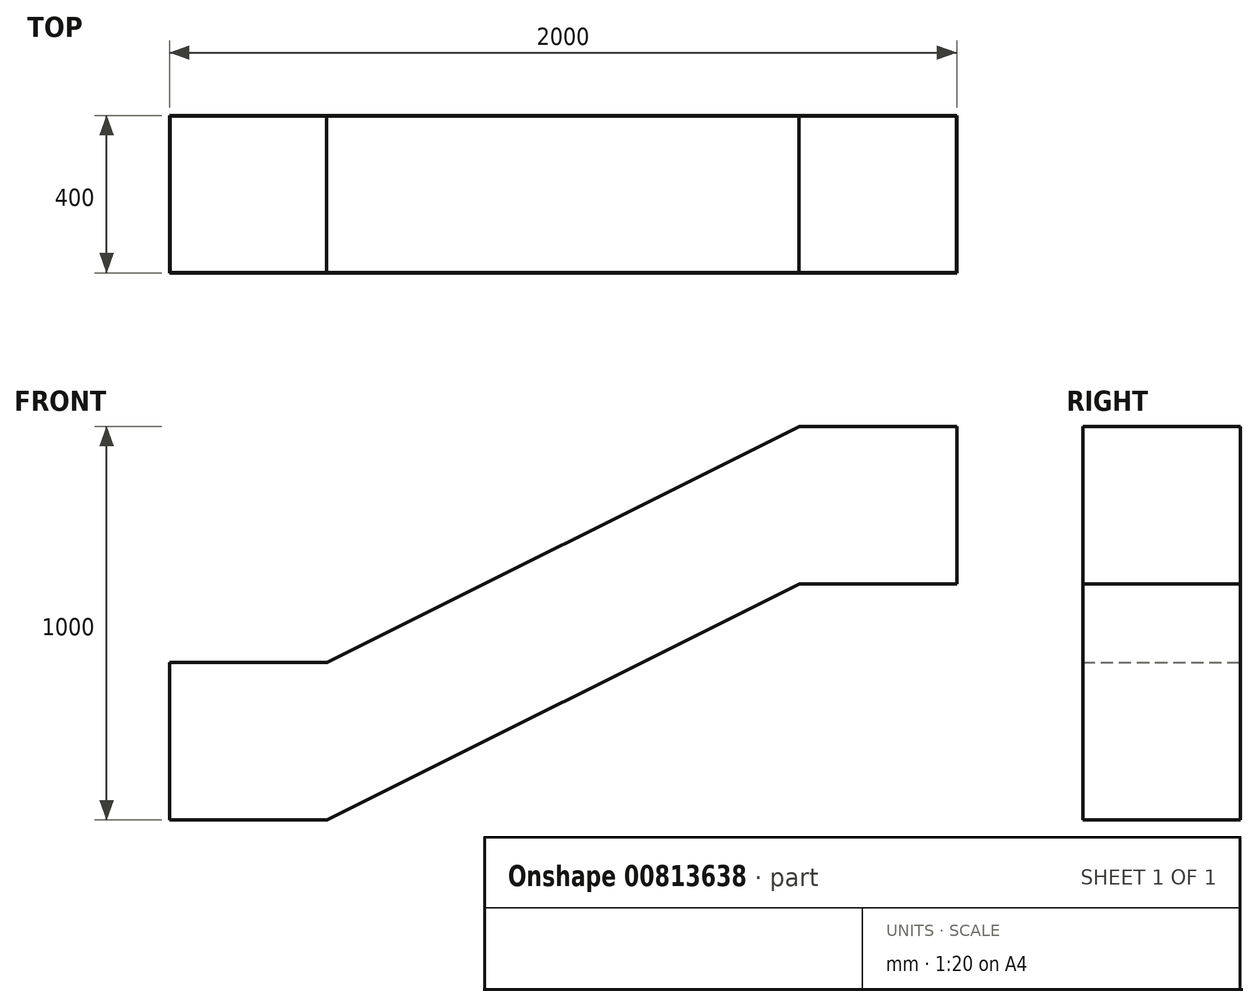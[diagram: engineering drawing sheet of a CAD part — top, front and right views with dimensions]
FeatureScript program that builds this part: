
annotation { "Feature Type Name" : "Feature", "Feature Type Description" : "" }
export const myFeature = defineFeature(function(context is Context, id is Id, definition is map)
    precondition{}
    {
        {
            var Q0;
            Q0=qCreatedBy(makeId("Front.planeOp"),FACE);
            var sketch = newSketch(context, id + "F0", { "sketchPlane" : qUnion([Q0])});
            skLineSegment(sketch, "E0", {"start": v(0, 0) * mm, "end": v(400, 0) * mm});
            skLineSegment(sketch, "E1", {"start": v(400, 0) * mm, "end": v(1600, 600) * mm});
            skLineSegment(sketch, "E2", {"start": v(1600, 600) * mm, "end": v(2000, 600) * mm});
            skLineSegment(sketch, "E3.0", {"start": v(0, 400) * mm, "end": v(400, 400) * mm});
            skLineSegment(sketch, "E4", {"start": v(2000, 1000) * mm, "end": v(2000, 600) * mm});
            skLineSegment(sketch, "E5", {"start": v(0, 400) * mm, "end": v(0, 0) * mm});
            skLineSegment(sketch, "E6", {"start": v(2000, 1000) * mm, "end": v(1600, 1000) * mm});
            skLineSegment(sketch, "E7", {"start": v(400, 400) * mm, "end": v(1600, 1000) * mm});
            skSolve(sketch);
        }
        {
            var Q0;
            Q0=makeQuery(id+"F0.imprint","IMPRINT",FACE,{"disambiguationData":[TD([[makeQuery(id+"F0.imprint","IMPRINT",EDGE,{"derivedFrom":sQuery(id+"F0.wireOp",EDGE,"E0")}),1.0]])]});
            extrude(context, id + "F1", {"entities" : qUnion([Q0]), "depth" : 400 * mm, "offsetDistance" : 25 * mm});
        }
        {
            var Q0;
            Q0=makeQuery(id+"F1.opExtrude","SWEPT_FACE",FACE,{"disambiguationData":[OSD([sQuery(id+"F0.wireOp",EDGE,"E3.0")])]});
            var Q1;
            Q1=makeQuery(id+"F1.opExtrude","SWEPT_FACE",FACE,{"disambiguationData":[OSD([sQuery(id+"F0.wireOp",EDGE,"E7")])]});
            var Q2;
            Q2=makeQuery(id+"F1.opExtrude","SWEPT_FACE",FACE,{"disambiguationData":[OSD([sQuery(id+"F0.wireOp",EDGE,"E6")])]});
            shell(context, id + "F2", {"entities" : qUnion([Q0, Q1, Q2]), "thickness" : 1 * mm});
        }
    });
